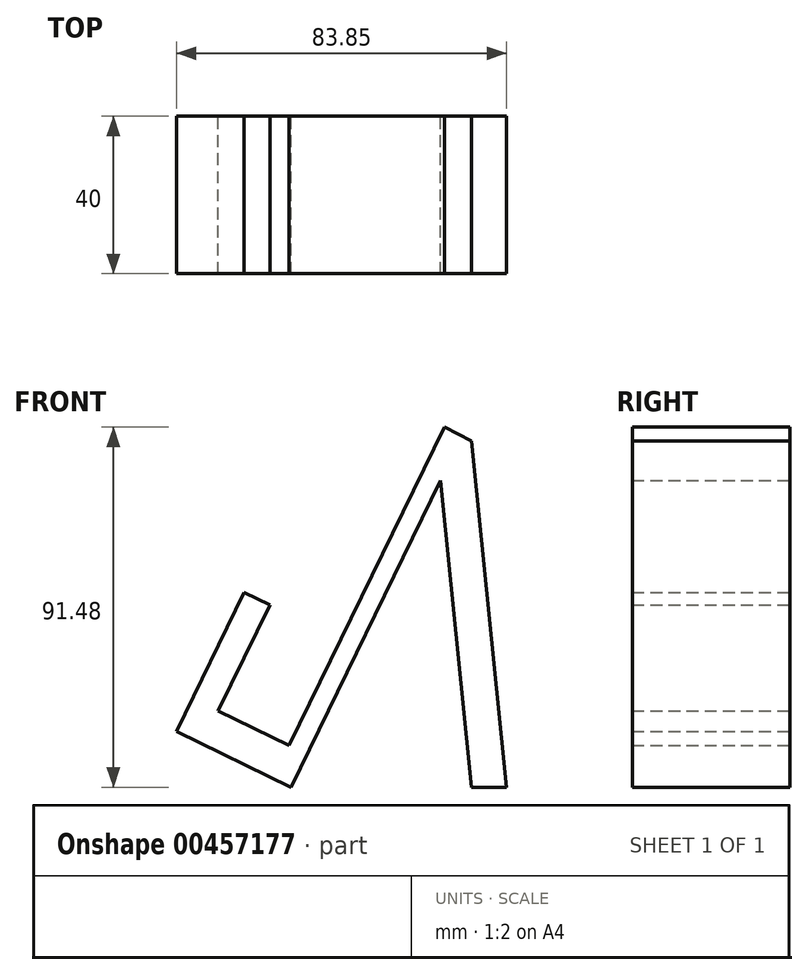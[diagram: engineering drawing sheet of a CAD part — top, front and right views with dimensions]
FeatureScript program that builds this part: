
annotation { "Feature Type Name" : "Feature", "Feature Type Description" : "" }
export const myFeature = defineFeature(function(context is Context, id is Id, definition is map)
    precondition{}
    {
        {
            var Q0;
            Q0=qCreatedBy(makeId("Front.planeOp"),FACE);
            var sketch = newSketch(context, id + "F0", { "sketchPlane" : qUnion([Q0])});
            skLineSegment(sketch, "E0", {"start": v(-39.43, -84.51) * mm, "end": v(0, -3.61) * mm});
            skLineSegment(sketch, "E1", {"start": v(-39.43, -84.51) * mm, "end": v(-57.4, -75.75) * mm});
            skLineSegment(sketch, "E2", {"start": v(-57.4, -75.75) * mm, "end": v(-44.27, -48.78) * mm});
            skLineSegment(sketch, "E3", {"start": v(-44.27, -48.78) * mm, "end": v(-50.84, -45.58) * mm});
            skPoint(sketch, "E3.endSnap0", {"position": v(-50.84, -62.27) * mm});
            skLineSegment(sketch, "E4", {"start": v(-50.84, -45.58) * mm, "end": v(-68.06, -80.92) * mm});
            skLineSegment(sketch, "E5", {"start": v(-68.06, -80.92) * mm, "end": v(-38.99, -95.1) * mm});
            skLineSegment(sketch, "E6", {"start": v(6.9, -7.17) * mm, "end": v(0, -3.61) * mm});
            skLineSegment(sketch, "E7", {"start": v(-38.99, -95.1) * mm, "end": v(-1, -17.15) * mm});
            skLineSegment(sketch, "E8", {"start": v(-38.99, -95.1) * mm, "end": v(48.55, -95.1) * mm, "construction": true});
            skLineSegment(sketch, "E9", {"start": v(-1, -17.15) * mm, "end": v(6.9, -95.1) * mm});
            skLineSegment(sketch, "E10", {"start": v(6.9, -7.17) * mm, "end": v(15.8, -95.1) * mm});
            skLineSegment(sketch, "E11", {"start": v(15.8, -95.1) * mm, "end": v(6.9, -95.1) * mm});
            skSolve(sketch);
        }
        {
            var Q0;
            Q0=makeQuery(id+"F0.imprint","IMPRINT",FACE,{"disambiguationData":[TD([[makeQuery(id+"F0.imprint","IMPRINT",EDGE,{"derivedFrom":sQuery(id+"F0.wireOp",EDGE,"E0")}),-1.0]])]});
            extrude(context, id + "F1", {"entities" : qUnion([Q0]), "depth" : 40 * mm});
        }
    });
